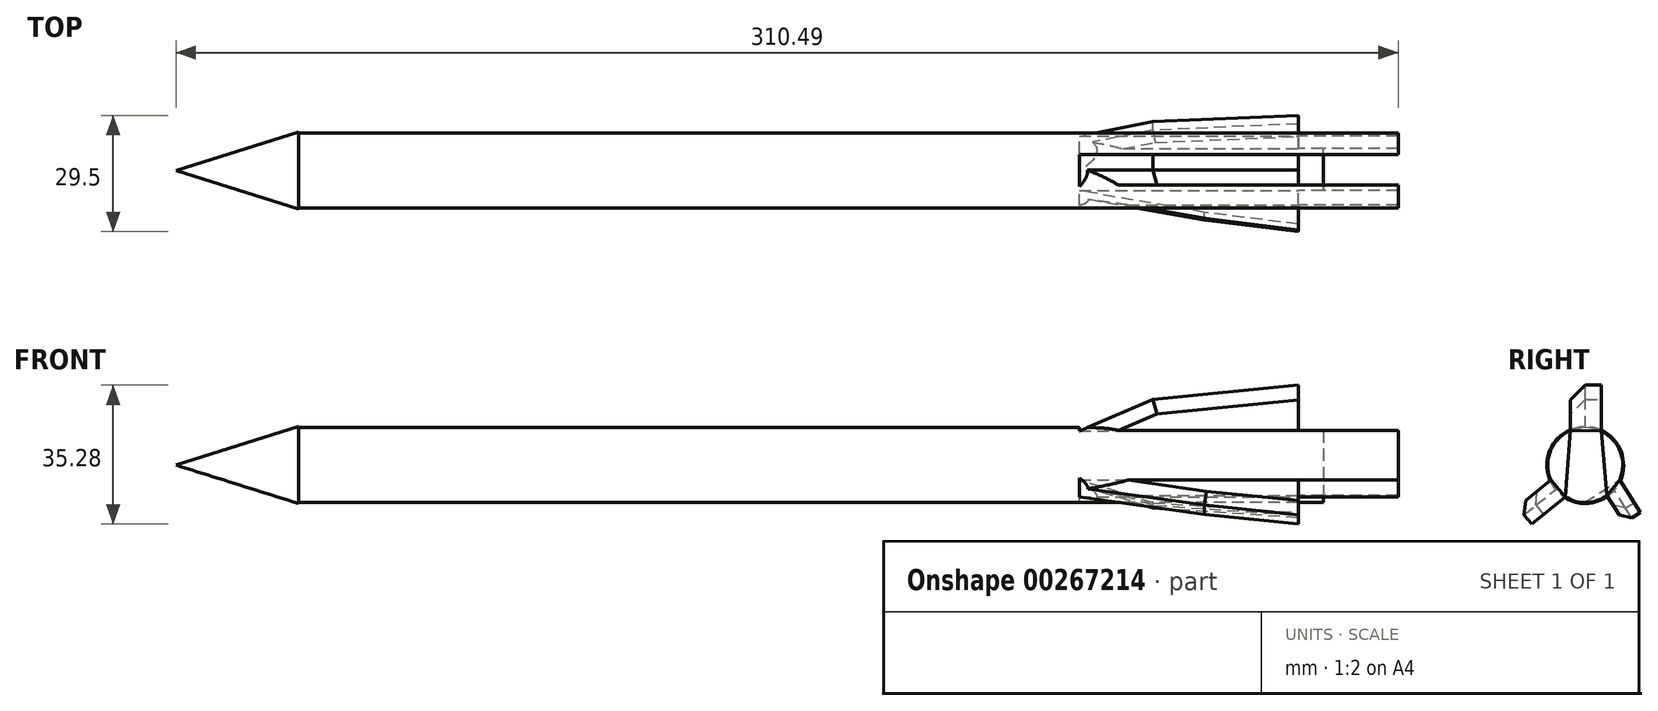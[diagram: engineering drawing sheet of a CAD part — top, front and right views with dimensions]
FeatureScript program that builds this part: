
annotation { "Feature Type Name" : "Feature", "Feature Type Description" : "" }
export const myFeature = defineFeature(function(context is Context, id is Id, definition is map)
    precondition{}
    {
        {
            var Q0;
            Q0=qCreatedBy(makeId("Right.planeOp"),FACE);
            var sketch = newSketch(context, id + "F0", { "sketchPlane" : qUnion([Q0])});
            skCircle(sketch, "E0", {"center": v(0, 0) * mm, "radius": 9.53 * mm});
            skSolve(sketch);
        }
        {
            var Q0;
            Q0=makeQuery(id+"F0.imprint","IMPRINT",FACE,{"disambiguationData":[TD([[makeQuery(id+"F0.imprint","IMPRINT",EDGE,{"derivedFrom":sQuery(id+"F0.wireOp",EDGE,"E0")}),1.0]])]});
            extrude(context, id + "F1", {"entities" : qUnion([Q0]), "depth" : 254 * mm});
        }
        {
            var Q0;
            Q0=qCreatedBy(makeId("Front.planeOp"),FACE);
            var sketch = newSketch(context, id + "F2", { "sketchPlane" : qUnion([Q0])});
            skLineSegment(sketch, "E1", {"start": v(0, 0) * mm, "end": v(-31.09, 0) * mm});
            skLineSegment(sketch, "E2", {"start": v(-31.09, 0) * mm, "end": v(0, -9.75) * mm});
            skLineSegment(sketch, "E3", {"start": v(0, -9.75) * mm, "end": v(0, 0) * mm});
            skSolve(sketch);
        }
        {
            var Q0;
            Q0=makeQuery(id+"F2.imprint","IMPRINT",FACE,{"disambiguationData":[TD([[makeQuery(id+"F2.imprint","IMPRINT",EDGE,{"derivedFrom":sQuery(id+"F2.wireOp",EDGE,"E1")}),1.0]])]});
            var Q1;
            Q1=sQuery(id+"F2.wireOp",EDGE,"E1");
            revolve(context, id + "F3", {"operationType" : NewBodyOperationType.ADD, "entities" : qUnion([Q0]), "axis" : qUnion([Q1]), "revolveType" : RevolveType.FULL});
        }
        {
            var Q0;
            Q0=makeQuery(id+"F1.opExtrude","CAP_FACE",FACE,{"disambiguationData":[OSD([sQuery(id+"F0.wireOp",EDGE,"E0")])],"isStart":false});
            var sketch = newSketch(context, id + "F4", { "sketchPlane" : qUnion([Q0])});
            skLineSegment(sketch, "E4", {"start": v(4.06, 8.62) * mm, "end": v(4.06, 20.31) * mm});
            skLineSegment(sketch, "E5", {"start": v(4.06, 20.31) * mm, "end": v(-3.73, 20.31) * mm});
            skLineSegment(sketch, "E6", {"start": v(-3.73, 20.31) * mm, "end": v(-3.73, 8.76) * mm});
            skLineSegment(sketch, "E7", {"start": v(-8.72, -3.83) * mm, "end": v(-17.13, -10.65) * mm});
            skLineSegment(sketch, "E8", {"start": v(-17.13, -10.65) * mm, "end": v(-13.62, -14.97) * mm});
            skLineSegment(sketch, "E9", {"start": v(-13.62, -14.97) * mm, "end": v(-5.1, -8.05) * mm});
            skLineSegment(sketch, "E10", {"start": v(8.73, -3.8) * mm, "end": v(13.97, -12.05) * mm});
            skLineSegment(sketch, "E11", {"start": v(13.97, -12.05) * mm, "end": v(9.9, -14.64) * mm});
            skLineSegment(sketch, "E12", {"start": v(9.9, -14.64) * mm, "end": v(5.53, -7.76) * mm});
            skSolve(sketch);
        }
        {
            var Q0;
            {var subQ0=sQuery(id+"F4.wireOp",EDGE,"E4");Q0=makeQuery(id+"F4.imprint","IMPRINT",FACE,{"disambiguationData":[TD([[makeQuery(id+"F4.imprint","IMPRINT",EDGE,{"derivedFrom":subQ0}),1.0]])]});}
            var Q1;
            {var subQ0=sQuery(id+"F4.wireOp",EDGE,"E7");Q1=makeQuery(id+"F4.imprint","IMPRINT",FACE,{"disambiguationData":[TD([[makeQuery(id+"F4.imprint","IMPRINT",EDGE,{"derivedFrom":subQ0}),1.0]])]});}
            var Q2;
            {var subQ0=sQuery(id+"F4.wireOp",EDGE,"E10");Q2=makeQuery(id+"F4.imprint","IMPRINT",FACE,{"disambiguationData":[TD([[makeQuery(id+"F4.imprint","IMPRINT",EDGE,{"derivedFrom":subQ0}),-1.0]])]});}
            extrude(context, id + "F5", {"entities" : qUnion([Q0, Q1, Q2]), "operationType" : NewBodyOperationType.ADD, "oppositeDirection" : true, "depth" : 55.63 * mm});
        }
        {
            var Q0;
            {var subQ0=sQuery(id+"F0.wireOp",EDGE,"E0");Q0=makeQuery(id+"F5.boolean.opBoolean","MERGE",FACE,{"derivedFrom":[makeQuery(id+"F1.opExtrude","CAP_FACE",FACE,{"disambiguationData":[OSD([subQ0])],"isStart":false}),makeQuery(id+"F5.opExtrude","CAP_FACE",FACE,{"disambiguationData":[OSD([subQ0,sQuery(id+"F4.wireOp",EDGE,"E4"),sQuery(id+"F4.wireOp",EDGE,"E5"),sQuery(id+"F4.wireOp",EDGE,"E6")])],"isStart":true}),makeQuery(id+"F5.opExtrude","CAP_FACE",FACE,{"disambiguationData":[OSD([subQ0,sQuery(id+"F4.wireOp",EDGE,"E7"),sQuery(id+"F4.wireOp",EDGE,"E8"),sQuery(id+"F4.wireOp",EDGE,"E9")])],"isStart":true}),makeQuery(id+"F5.opExtrude","CAP_FACE",FACE,{"disambiguationData":[OSD([subQ0,sQuery(id+"F4.wireOp",EDGE,"E10"),sQuery(id+"F4.wireOp",EDGE,"E11"),sQuery(id+"F4.wireOp",EDGE,"E12")])],"isStart":true})]});}
            var sketch = newSketch(context, id + "F6", { "sketchPlane" : qUnion([Q0])});
            skLineSegment(sketch, "E13", {"start": v(-3.73, 8.76) * mm, "end": v(-8.86, 3.5) * mm});
            skLineSegment(sketch, "E14", {"start": v(-8.86, 3.5) * mm, "end": v(-8.72, -3.83) * mm});
            skLineSegment(sketch, "E15", {"start": v(-8.72, -3.83) * mm, "end": v(-5.1, -8.05) * mm});
            skLineSegment(sketch, "E16", {"start": v(-5.1, -8.05) * mm, "end": v(5.53, -7.76) * mm});
            skLineSegment(sketch, "E17", {"start": v(5.53, -7.76) * mm, "end": v(8.73, -3.8) * mm});
            skLineSegment(sketch, "E18", {"start": v(8.73, -3.8) * mm, "end": v(8.73, 3.8) * mm});
            skLineSegment(sketch, "E19", {"start": v(8.73, 3.8) * mm, "end": v(4.06, 8.62) * mm});
            skLineSegment(sketch, "E20", {"start": v(4.06, 8.62) * mm, "end": v(-3.73, 8.76) * mm});
            skLineSegment(sketch, "E21", {"start": v(-3.73, 8.76) * mm, "end": v(-5.1, -8.05) * mm});
            skLineSegment(sketch, "E22", {"start": v(4.06, 8.62) * mm, "end": v(5.53, -7.76) * mm});
            skSolve(sketch);
        }
        {
            var Q0;
            Q0=makeQuery(id+"F6.imprint","IMPRINT",FACE,{"disambiguationData":[TD([[makeQuery(id+"F6.imprint","IMPRINT",EDGE,{"derivedFrom":sQuery(id+"F6.wireOp",EDGE,"E16")}),1.0]])]});
            var Q1;
            Q1=makeQuery(id+"F6.imprint","IMPRINT",FACE,{"disambiguationData":[TD([[makeQuery(id+"F6.imprint","IMPRINT",EDGE,{"derivedFrom":sQuery(id+"F6.wireOp",EDGE,"E16")}),-1.0]])]});
            extrude(context, id + "F7", {"entities" : qUnion([Q0, Q1]), "operationType" : NewBodyOperationType.ADD, "depth" : 6.35 * mm});
        }
        {
            var Q0;
            Q0=makeQuery(id+"F6.imprint","IMPRINT",FACE,{"disambiguationData":[TD([[makeQuery(id+"F6.imprint","IMPRINT",EDGE,{"derivedFrom":sQuery(id+"F6.wireOp",EDGE,"E13")}),1.0]])]});
            var Q1;
            Q1=makeQuery(id+"F6.imprint","IMPRINT",FACE,{"disambiguationData":[TD([[makeQuery(id+"F6.imprint","IMPRINT",EDGE,{"derivedFrom":sQuery(id+"F6.wireOp",EDGE,"E17")}),1.0]])]});
            var Q2;
            {var subQ0=sQuery(id+"F6.wireOp",EDGE,"E18");Q2=makeQuery(id+"F6.imprint","IMPRINT",FACE,{"disambiguationData":[TD([[makeQuery(id+"F6.imprint","IMPRINT",EDGE,{"derivedFrom":subQ0}),-1.0]])]});}
            var Q3;
            {var subQ0=sQuery(id+"F6.wireOp",EDGE,"E19");Q3=makeQuery(id+"F6.imprint","IMPRINT",FACE,{"disambiguationData":[TD([[makeQuery(id+"F6.imprint","IMPRINT",EDGE,{"derivedFrom":subQ0}),-1.0]])]});}
            var Q4;
            {var subQ0=sQuery(id+"F6.wireOp",EDGE,"E14");Q4=makeQuery(id+"F6.imprint","IMPRINT",FACE,{"disambiguationData":[TD([[makeQuery(id+"F6.imprint","IMPRINT",EDGE,{"derivedFrom":subQ0}),-1.0]])]});}
            var Q5;
            {var subQ0=sQuery(id+"F6.wireOp",EDGE,"E13");Q5=makeQuery(id+"F6.imprint","IMPRINT",FACE,{"disambiguationData":[TD([[makeQuery(id+"F6.imprint","IMPRINT",EDGE,{"derivedFrom":subQ0}),-1.0]])]});}
            extrude(context, id + "F8", {"entities" : qUnion([Q0, Q1, Q2, Q3, Q4, Q5]), "operationType" : NewBodyOperationType.ADD, "depth" : 25.4 * mm});
        }
        {
            var Q0;
            Q0=makeQuery(id+"F5.opExtrude","SWEPT_FACE",FACE,{"disambiguationData":[OSD([sQuery(id+"F4.wireOp",EDGE,"E4")])]});
            var sketch = newSketch(context, id + "F9", { "sketchPlane" : qUnion([Q0])});
            skLineSegment(sketch, "E23", {"start": v(-198.37, 8.62) * mm, "end": v(-217.17, 16.66) * mm});
            skLineSegment(sketch, "E24", {"start": v(-217.17, 16.66) * mm, "end": v(-254, 20.31) * mm});
            skLineSegment(sketch, "E25", {"start": v(-254, 20.31) * mm, "end": v(-254, 8.62) * mm});
            skLineSegment(sketch, "E26", {"start": v(-254, 8.62) * mm, "end": v(-198.37, 8.62) * mm});
            skSolve(sketch);
        }
        {
            var Q0;
            Q0=makeQuery(id+"F9.imprint","IMPRINT",FACE,{"disambiguationData":[TD([[makeQuery(id+"F9.imprint","IMPRINT",EDGE,{"derivedFrom":sQuery(id+"F9.wireOp",EDGE,"E23")}),-1.0]])]});
            extrude(context, id + "F10", {"entities" : qUnion([Q0]), "operationType" : NewBodyOperationType.REMOVE, "oppositeDirection" : true, "depth" : 25.4 * mm});
        }
        {
            var Q0;
            Q0=makeQuery(id+"F5.opExtrude","SWEPT_FACE",FACE,{"disambiguationData":[OSD([sQuery(id+"F4.wireOp",EDGE,"E10")])]});
            var sketch = newSketch(context, id + "F11", { "sketchPlane" : qUnion([Q0])});
            skLineSegment(sketch, "E27", {"start": v(-217.15, -14.72) * mm, "end": v(-254, -17.67) * mm});
            skLineSegment(sketch, "E28", {"start": v(-254, -17.67) * mm, "end": v(-254, -7.9) * mm});
            skLineSegment(sketch, "E29", {"start": v(-254, -7.9) * mm, "end": v(-198.37, -7.9) * mm});
            skLineSegment(sketch, "E30", {"start": v(-217.15, -14.72) * mm, "end": v(-198.37, -7.9) * mm});
            skSolve(sketch);
        }
        {
            var Q0;
            Q0=makeQuery(id+"F11.imprint","IMPRINT",FACE,{"disambiguationData":[TD([[makeQuery(id+"F11.imprint","IMPRINT",EDGE,{"derivedFrom":sQuery(id+"F11.wireOp",EDGE,"40ponUIR-AfOa-7Bsa-l0FT-jTZB9G8GWVhF")}),1.0]])]});
            var Q1;
            Q1=makeQuery(id+"F11.imprint","IMPRINT",FACE,{"disambiguationData":[TD([[makeQuery(id+"F11.imprint","IMPRINT",EDGE,{"derivedFrom":sQuery(id+"F11.wireOp",EDGE,"E27")}),1.0]])]});
            extrude(context, id + "F12", {"entities" : qUnion([Q0, Q1]), "operationType" : NewBodyOperationType.REMOVE, "oppositeDirection" : true, "depth" : 25.4 * mm});
        }
        {
            var Q0;
            Q0=makeQuery(id+"F5.opExtrude","SWEPT_FACE",FACE,{"disambiguationData":[OSD([sQuery(id+"F4.wireOp",EDGE,"E9")])]});
            var sketch = newSketch(context, id + "F13", { "sketchPlane" : qUnion([Q0])});
            skLineSegment(sketch, "E31", {"start": v(254, 20.01) * mm, "end": v(230.17, 16.14) * mm});
            skLineSegment(sketch, "E32", {"start": v(230.17, 16.14) * mm, "end": v(198.37, 9.03) * mm});
            skLineSegment(sketch, "E33", {"start": v(198.37, 9.03) * mm, "end": v(254, 9.03) * mm});
            skLineSegment(sketch, "E34", {"start": v(254, 9.03) * mm, "end": v(254, 20.01) * mm});
            skSolve(sketch);
        }
        {
            var Q0;
            Q0=makeQuery(id+"F13.imprint","IMPRINT",FACE,{"disambiguationData":[TD([[makeQuery(id+"F13.imprint","IMPRINT",EDGE,{"derivedFrom":sQuery(id+"F13.wireOp",EDGE,"E31")}),-1.0]])]});
            extrude(context, id + "F14", {"entities" : qUnion([Q0]), "operationType" : NewBodyOperationType.REMOVE, "oppositeDirection" : true, "depth" : 25.4 * mm});
        }
        {
            var Q0;
            Q0=makeQuery(id+"F10.boolean.opBoolean","COPY",EDGE,{"derivedFrom":makeQuery(id+"F10.opExtrude","CAP_EDGE",EDGE,{"disambiguationData":[OSD([sQuery(id+"F9.wireOp",EDGE,"E23")])],"isStart":true})});
            var Q1;
            Q1=makeQuery(id+"F10.boolean.opBoolean","INTERSECT",EDGE,{"derivedFrom":[makeQuery(id+"F5.opExtrude","SWEPT_FACE",FACE,{"disambiguationData":[OSD([sQuery(id+"F4.wireOp",EDGE,"E6")])]}),makeQuery(id+"F10.opExtrude","SWEPT_FACE",FACE,{"disambiguationData":[OSD([sQuery(id+"F9.wireOp",EDGE,"E23")])]})]});
            var Q2;
            Q2=makeQuery(id+"F10.boolean.opBoolean","COPY",EDGE,{"derivedFrom":makeQuery(id+"F10.opExtrude","CAP_EDGE",EDGE,{"disambiguationData":[OSD([sQuery(id+"F9.wireOp",EDGE,"E24")])],"isStart":true})});
            var Q3;
            Q3=makeQuery(id+"F10.boolean.opBoolean","INTERSECT",EDGE,{"derivedFrom":[makeQuery(id+"F5.opExtrude","SWEPT_FACE",FACE,{"disambiguationData":[OSD([sQuery(id+"F4.wireOp",EDGE,"E6")])]}),makeQuery(id+"F10.opExtrude","SWEPT_FACE",FACE,{"disambiguationData":[OSD([sQuery(id+"F9.wireOp",EDGE,"E24")])]})]});
            chamfer(context, id + "F15", {"entities" : qUnion([Q0, Q1, Q2, Q3]), "width" : 3.8 * mm, "tangentPropagation" : true});
        }
        {
            var Q0;
            Q0=makeQuery(id+"F12.boolean.opBoolean","INTERSECT",EDGE,{"derivedFrom":[makeQuery(id+"F5.opExtrude","SWEPT_FACE",FACE,{"disambiguationData":[OSD([sQuery(id+"F4.wireOp",EDGE,"E12")])]}),makeQuery(id+"F12.opExtrude","SWEPT_FACE",FACE,{"disambiguationData":[OSD([sQuery(id+"F11.wireOp",EDGE,"E30")])]})]});
            var Q1;
            Q1=makeQuery(id+"F12.boolean.opBoolean","COPY",EDGE,{"derivedFrom":makeQuery(id+"F12.opExtrude","CAP_EDGE",EDGE,{"disambiguationData":[OSD([sQuery(id+"F11.wireOp",EDGE,"E30")])],"isStart":true})});
            var Q2;
            Q2=makeQuery(id+"F12.boolean.opBoolean","INTERSECT",EDGE,{"derivedFrom":[makeQuery(id+"F5.opExtrude","SWEPT_FACE",FACE,{"disambiguationData":[OSD([sQuery(id+"F4.wireOp",EDGE,"E12")])]}),makeQuery(id+"F12.opExtrude","SWEPT_FACE",FACE,{"disambiguationData":[OSD([sQuery(id+"F11.wireOp",EDGE,"E27")])]})]});
            var Q3;
            Q3=makeQuery(id+"F12.boolean.opBoolean","COPY",EDGE,{"derivedFrom":makeQuery(id+"F12.opExtrude","CAP_EDGE",EDGE,{"disambiguationData":[OSD([sQuery(id+"F11.wireOp",EDGE,"E27")])],"isStart":true})});
            chamfer(context, id + "F16", {"entities" : qUnion([Q0, Q1, Q2, Q3]), "width" : 2.3 * mm, "tangentPropagation" : true});
        }
        {
            var Q0;
            Q0=makeQuery(id+"F14.boolean.opBoolean","COPY",EDGE,{"derivedFrom":makeQuery(id+"F14.opExtrude","CAP_EDGE",EDGE,{"disambiguationData":[OSD([sQuery(id+"F13.wireOp",EDGE,"E32")])],"isStart":true})});
            var Q1;
            Q1=makeQuery(id+"F14.boolean.opBoolean","INTERSECT",EDGE,{"derivedFrom":[makeQuery(id+"F5.opExtrude","SWEPT_FACE",FACE,{"disambiguationData":[OSD([sQuery(id+"F4.wireOp",EDGE,"E7")])]}),makeQuery(id+"F14.opExtrude","SWEPT_FACE",FACE,{"disambiguationData":[OSD([sQuery(id+"F13.wireOp",EDGE,"E32")])]})]});
            var Q2;
            Q2=makeQuery(id+"F14.boolean.opBoolean","COPY",EDGE,{"derivedFrom":makeQuery(id+"F14.opExtrude","CAP_EDGE",EDGE,{"disambiguationData":[OSD([sQuery(id+"F13.wireOp",EDGE,"E31")])],"isStart":true})});
            var Q3;
            Q3=makeQuery(id+"F14.boolean.opBoolean","INTERSECT",EDGE,{"derivedFrom":[makeQuery(id+"F5.opExtrude","SWEPT_FACE",FACE,{"disambiguationData":[OSD([sQuery(id+"F4.wireOp",EDGE,"E7")])]}),makeQuery(id+"F14.opExtrude","SWEPT_FACE",FACE,{"disambiguationData":[OSD([sQuery(id+"F13.wireOp",EDGE,"E31")])]})]});
            chamfer(context, id + "F17", {"entities" : qUnion([Q0, Q1, Q2, Q3]), "width" : 2.54 * mm, "tangentPropagation" : true});
        }
    });
